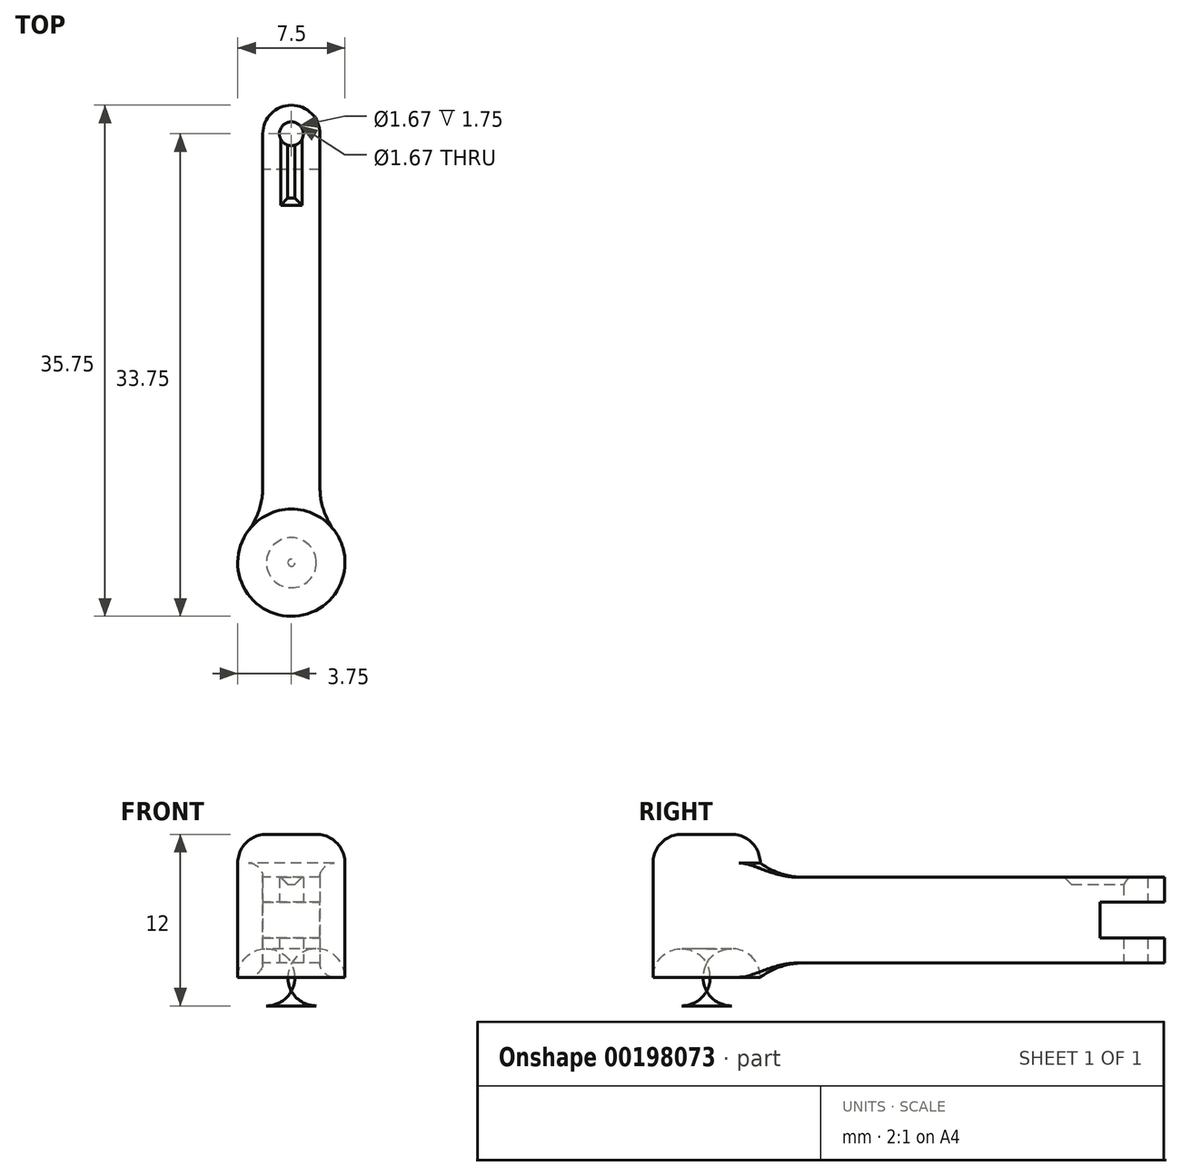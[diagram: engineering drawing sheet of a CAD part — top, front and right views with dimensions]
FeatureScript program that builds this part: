
annotation { "Feature Type Name" : "Feature", "Feature Type Description" : "" }
export const myFeature = defineFeature(function(context is Context, id is Id, definition is map)
    precondition{}
    {
        {
            var Q0;
            Q0=qCreatedBy(makeId("Top.planeOp"),FACE);
            var sketch = newSketch(context, id + "F0", { "sketchPlane" : qUnion([Q0])});
            skArc(sketch, "E0", {"start": v(2, 0) * mm, "mid": v(0, 2) * mm, "end": v(-2, 0) * mm});
            skLineSegment(sketch, "E1", {"start": v(0, 0) * mm, "end": v(0, 3.9) * mm, "construction": true});
            skLineSegment(sketch, "E2", {"start": v(-2, 0) * mm, "end": v(-2, -30) * mm});
            skLineSegment(sketch, "E3.MirrorCS", {"start": v(2, 0) * mm, "end": v(2, -30) * mm});
            skArc(sketch, "E4", {"start": v(-2, -30) * mm, "mid": v(0, -32) * mm, "end": v(2, -30) * mm});
            skCircle(sketch, "E5", {"center": v(0, 0) * mm, "radius": 0.84 * mm});
            skSolve(sketch);
        }
        {
            var Q0;
            Q0 = qSketchRegion(id + "F0", true);
            extrude(context, id + "F1", {"entities" : qUnion([Q0]), "endBound" : BoundingType.SYMMETRIC, "depth" : 6 * mm});
        }
        {
            var Q0;
            Q0=makeQuery(id+"F1.opExtrude","SWEPT_FACE",FACE,{"disambiguationData":[OSD([sQuery(id+"F0.wireOp",EDGE,"E2")])]});
            var sketch = newSketch(context, id + "F2", { "sketchPlane" : qUnion([Q0])});
            skLineSegment(sketch, "E6.0", {"start": v(-0.84, 3) * mm, "end": v(0.84, 3) * mm, "construction": true});
            skLineSegment(sketch, "E7.bottom", {"start": v(-2.5, 1.25) * mm, "end": v(2.5, 1.25) * mm});
            skLineSegment(sketch, "E7.top", {"start": v(-2.5, -1.25) * mm, "end": v(2.5, -1.25) * mm});
            skLineSegment(sketch, "E7.left", {"start": v(-2.5, 1.25) * mm, "end": v(-2.5, -1.25) * mm});
            skLineSegment(sketch, "E7.right", {"start": v(2.5, 1.25) * mm, "end": v(2.5, -1.25) * mm});
            skSolve(sketch);
        }
        {
            var Q0;
            Q0 = qSketchRegion(id + "F2", true);
            extrude(context, id + "F3", {"entities" : qUnion([Q0]), "operationType" : NewBodyOperationType.REMOVE, "endBound" : BoundingType.THROUGH_ALL, "oppositeDirection" : true, "depth" : 25 * mm});
        }
        {
            var Q0;
            Q0=makeQuery(id+"F1.opExtrude","CAP_FACE",FACE,{"disambiguationData":[OSD([sQuery(id+"F0.wireOp",EDGE,"E0"),sQuery(id+"F0.wireOp",EDGE,"E2"),sQuery(id+"F0.wireOp",EDGE,"E3.MirrorCS"),sQuery(id+"F0.wireOp",EDGE,"E4"),sQuery(id+"F0.wireOp",EDGE,"E5")])],"isStart":false});
            var sketch = newSketch(context, id + "F4", { "sketchPlane" : qUnion([Q0])});
            skLineSegment(sketch, "E8.bottom", {"start": v(-0.75, 0) * mm, "end": v(0.75, 0) * mm});
            skLineSegment(sketch, "E8.top", {"start": v(-0.75, -5) * mm, "end": v(0.75, -5) * mm});
            skLineSegment(sketch, "E8.left", {"start": v(-0.75, 0) * mm, "end": v(-0.75, -5) * mm});
            skLineSegment(sketch, "E8.right", {"start": v(0.75, 0) * mm, "end": v(0.75, -5) * mm});
            skSolve(sketch);
        }
        {
            var Q0;
            Q0 = qSketchRegion(id + "F4", true);
            extrude(context, id + "F5", {"entities" : qUnion([Q0]), "operationType" : NewBodyOperationType.REMOVE, "oppositeDirection" : true, "depth" : .5 * mm, "hasDraft" : true, "draftAngle" : 45 * degree, "draftPullDirection" : true});
        }
        {
            var Q0;
            Q0=makeQuery(id+"F1.opExtrude","CAP_FACE",FACE,{"disambiguationData":[OSD([sQuery(id+"F0.wireOp",EDGE,"E0"),sQuery(id+"F0.wireOp",EDGE,"E2"),sQuery(id+"F0.wireOp",EDGE,"E3.MirrorCS"),sQuery(id+"F0.wireOp",EDGE,"E4"),sQuery(id+"F0.wireOp",EDGE,"E5")])],"isStart":false});
            var Q1;
            Q1=makeQuery(id+"F1.opExtrude","CAP_FACE",FACE,{"disambiguationData":[OSD([sQuery(id+"F0.wireOp",EDGE,"E0"),sQuery(id+"F0.wireOp",EDGE,"E2"),sQuery(id+"F0.wireOp",EDGE,"E3.MirrorCS"),sQuery(id+"F0.wireOp",EDGE,"E4"),sQuery(id+"F0.wireOp",EDGE,"E5")])],"isStart":true});
            cPlane(context, id + "F6", {"entities" : qUnion([Q0, Q1]), "cplaneType" : CPlaneType.MID_PLANE, "offset" : 25 * mm, "width" : 150 * mm, "height" : 150 * mm});
        }
        {
            var Q0;
            Q0=makeQuery(id+"F1.opExtrude","CAP_FACE",FACE,{"disambiguationData":[OSD([sQuery(id+"F0.wireOp",EDGE,"E0"),sQuery(id+"F0.wireOp",EDGE,"E2"),sQuery(id+"F0.wireOp",EDGE,"E3.MirrorCS"),sQuery(id+"F0.wireOp",EDGE,"E4"),sQuery(id+"F0.wireOp",EDGE,"E5")])],"isStart":false});
            cPlane(context, id + "F7", {"entities" : qUnion([Q0]), "cplaneType" : CPlaneType.OFFSET, "offset" : 3 * mm, "width" : 150 * mm, "height" : 150 * mm});
        }
        {
            var Q0;
            Q0=qCreatedBy(id+"F7.planeOp",FACE);
            var sketch = newSketch(context, id + "F8", { "sketchPlane" : qUnion([Q0])});
            skCircle(sketch, "E9", {"center": v(0, -30) * mm, "radius": 3.75 * mm});
            skSolve(sketch);
        }
        {
            var Q0;
            Q0 = qSketchRegion(id + "F8", true);
            extrude(context, id + "F9", {"entities" : qUnion([Q0]), "operationType" : NewBodyOperationType.ADD, "oppositeDirection" : true, "depth" : 12 * mm});
        }
        {
            var Q0;
            Q0=makeQuery(id+"F9.boolean.opBoolean","INTERSECT",EDGE,{"derivedFrom":[makeQuery(id+"F1.opExtrude","SWEPT_FACE",FACE,{"disambiguationData":[OSD([sQuery(id+"F0.wireOp",EDGE,"E2")])]}),makeQuery(id+"F9.opExtrude","SWEPT_FACE",FACE,{"disambiguationData":[OSD([sQuery(id+"F8.wireOp",EDGE,"E9")])]})]});
            var Q1;
            Q1=makeQuery(id+"F9.boolean.opBoolean","INTERSECT",EDGE,{"derivedFrom":[makeQuery(id+"F1.opExtrude","SWEPT_FACE",FACE,{"disambiguationData":[OSD([sQuery(id+"F0.wireOp",EDGE,"E3.MirrorCS")])]}),makeQuery(id+"F9.opExtrude","SWEPT_FACE",FACE,{"disambiguationData":[OSD([sQuery(id+"F8.wireOp",EDGE,"E9")])]})]});
            fillet(context, id + "F10", {"entities" : qUnion([Q0, Q1]), "radius" : 5 * mm, "tangentPropagation" : true, "allowEdgeOverflow" : false});
        }
        {
            var Q0;
            Q0=makeQuery(id+"F9.opExtrude","CAP_FACE",FACE,{"disambiguationData":[OSD([sQuery(id+"F8.wireOp",EDGE,"E9")])],"isStart":true});
            var Q1;
            Q1=makeQuery(id+"F9.opExtrude","CAP_FACE",FACE,{"disambiguationData":[OSD([sQuery(id+"F8.wireOp",EDGE,"E9")])],"isStart":false});
            fillet(context, id + "F11", {"entities" : qUnion([Q0, Q1]), "radius" : 2 * mm, "tangentPropagation" : true, "allowEdgeOverflow" : false});
        }
        {
            var Q0;
            Q0=makeQuery(id+"F9.boolean.opBoolean","INTERSECT",EDGE,{"derivedFrom":[makeQuery(id+"F1.opExtrude","CAP_FACE",FACE,{"disambiguationData":[OSD([sQuery(id+"F0.wireOp",EDGE,"E0"),sQuery(id+"F0.wireOp",EDGE,"E2"),sQuery(id+"F0.wireOp",EDGE,"E3.MirrorCS"),sQuery(id+"F0.wireOp",EDGE,"E4"),sQuery(id+"F0.wireOp",EDGE,"E5")])],"isStart":false}),makeQuery(id+"F9.opExtrude","SWEPT_FACE",FACE,{"disambiguationData":[OSD([sQuery(id+"F8.wireOp",EDGE,"E9")])]})]});
            var Q1;
            Q1=makeQuery(id+"F9.boolean.opBoolean","INTERSECT",EDGE,{"derivedFrom":[makeQuery(id+"F1.opExtrude","CAP_FACE",FACE,{"disambiguationData":[OSD([sQuery(id+"F0.wireOp",EDGE,"E0"),sQuery(id+"F0.wireOp",EDGE,"E2"),sQuery(id+"F0.wireOp",EDGE,"E3.MirrorCS"),sQuery(id+"F0.wireOp",EDGE,"E4"),sQuery(id+"F0.wireOp",EDGE,"E5")])],"isStart":true}),makeQuery(id+"F9.opExtrude","SWEPT_FACE",FACE,{"disambiguationData":[OSD([sQuery(id+"F8.wireOp",EDGE,"E9")])]})]});
            fillet(context, id + "F12", {"entities" : qUnion([Q0, Q1]), "radius" : 5 * mm, "tangentPropagation" : true, "allowEdgeOverflow" : false});
        }
    });
